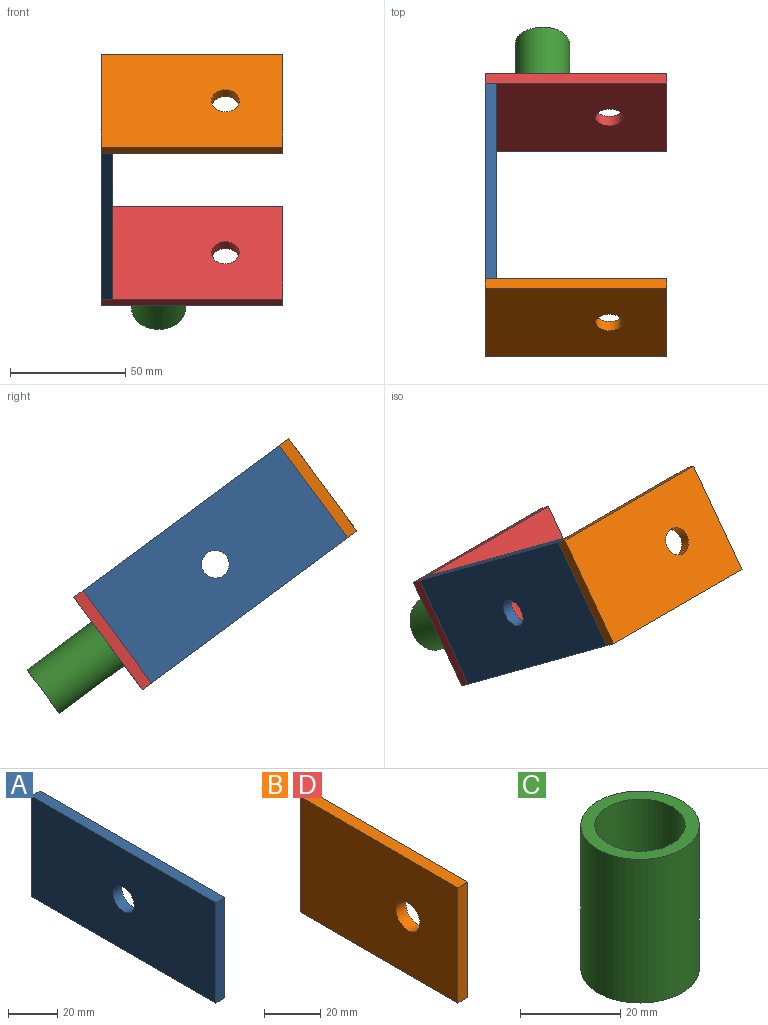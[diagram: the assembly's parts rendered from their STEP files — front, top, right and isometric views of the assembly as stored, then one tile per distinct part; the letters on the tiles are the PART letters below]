
ASSEMBLY  parts=4 mates=2
PART A: 7 faces, bbox 5x106x50 mm
  f0: plane 106x5mm, normal (0,0,1), area 530mm2, adj f1,f4,f5,f6
  f1: plane 50x5mm, normal (0,-1,0), area 250mm2, adj f0,f2,f5,f6
  f2: plane 106x5mm, normal (0,0,-1), area 530mm2, adj f1,f4,f5,f6
  f3: cylinder r=6mm len=12mm, axis (-1,0,0), area 188.5mm2, adj f5,f6
  f4: plane 50x5mm, normal (0,1,0), area 250mm2, adj f0,f2,f5,f6
  f5: plane 106x50mm, normal (1,0,0), area 5186.9mm2, adj f0,f1,f2,f3,f4
  f6: plane 106x50mm, normal (-1,0,0), area 5186.9mm2, adj f0,f1,f2,f3,f4
PART B: 7 faces, bbox 5x79x50 mm
  f0: plane 79x5mm, normal (0,0,1), area 395mm2, adj f1,f4,f5,f6
  f1: plane 50x5mm, normal (0,-1,0), area 250mm2, adj f0,f2,f5,f6
  f2: plane 79x5mm, normal (0,0,-1), area 395mm2, adj f1,f4,f5,f6
  f3: cylinder r=6mm len=12mm, axis (-1,0,0), area 188.5mm2, adj f5,f6
  f4: plane 50x5mm, normal (0,1,0), area 250mm2, adj f0,f2,f5,f6
  f5: plane 79x50mm, normal (1,0,0), area 3836.9mm2, adj f0,f1,f2,f3,f4
  f6: plane 79x50mm, normal (-1,0,0), area 3836.9mm2, adj f0,f1,f2,f3,f4
PART C: 4 faces, bbox 23.6x23.6x35 mm
  f0: plane 23.6x23.6mm, normal (0,0,1), area 183mm2, adj f1,f3
  f1: cylinder r=9mm len=35mm, axis (0,0,1), area 1979.2mm2, adj f0,f2
  f2: plane 23.6x23.6mm, normal (0,0,-1), area 183mm2, adj f1,f3
  f3: cylinder r=11.8mm len=35mm, axis (0,0,1), area 2595mm2, adj f0,f2
PART D: same geometry as B
PLACE A rot(axis=(-1,0,0),36.5deg) t=(-83.12,-123.13,-158.86)mm
PLACE B rot(axis=(0.69,-0.69,0.23),154.4deg) t=(-83.12,7.08,153.6)mm
PLACE C rot(axis=(1,0,0),53.5deg) t=(-58.12,48.63,-134.32)mm
PLACE D rot(axis=(-0.3,0.3,0.91),95.6deg) t=(-83.12,-49.18,-100.57)mm
MATE fastened D.f5 <-> C.f1  axis (0,-0.8,0.59) through (-58.12,25.57,-7.99)mm
MATE fastened A.f1 <-> B.f6  axis (0,0.8,-0.59) through (-83.12,-78.52,37.95)mm
